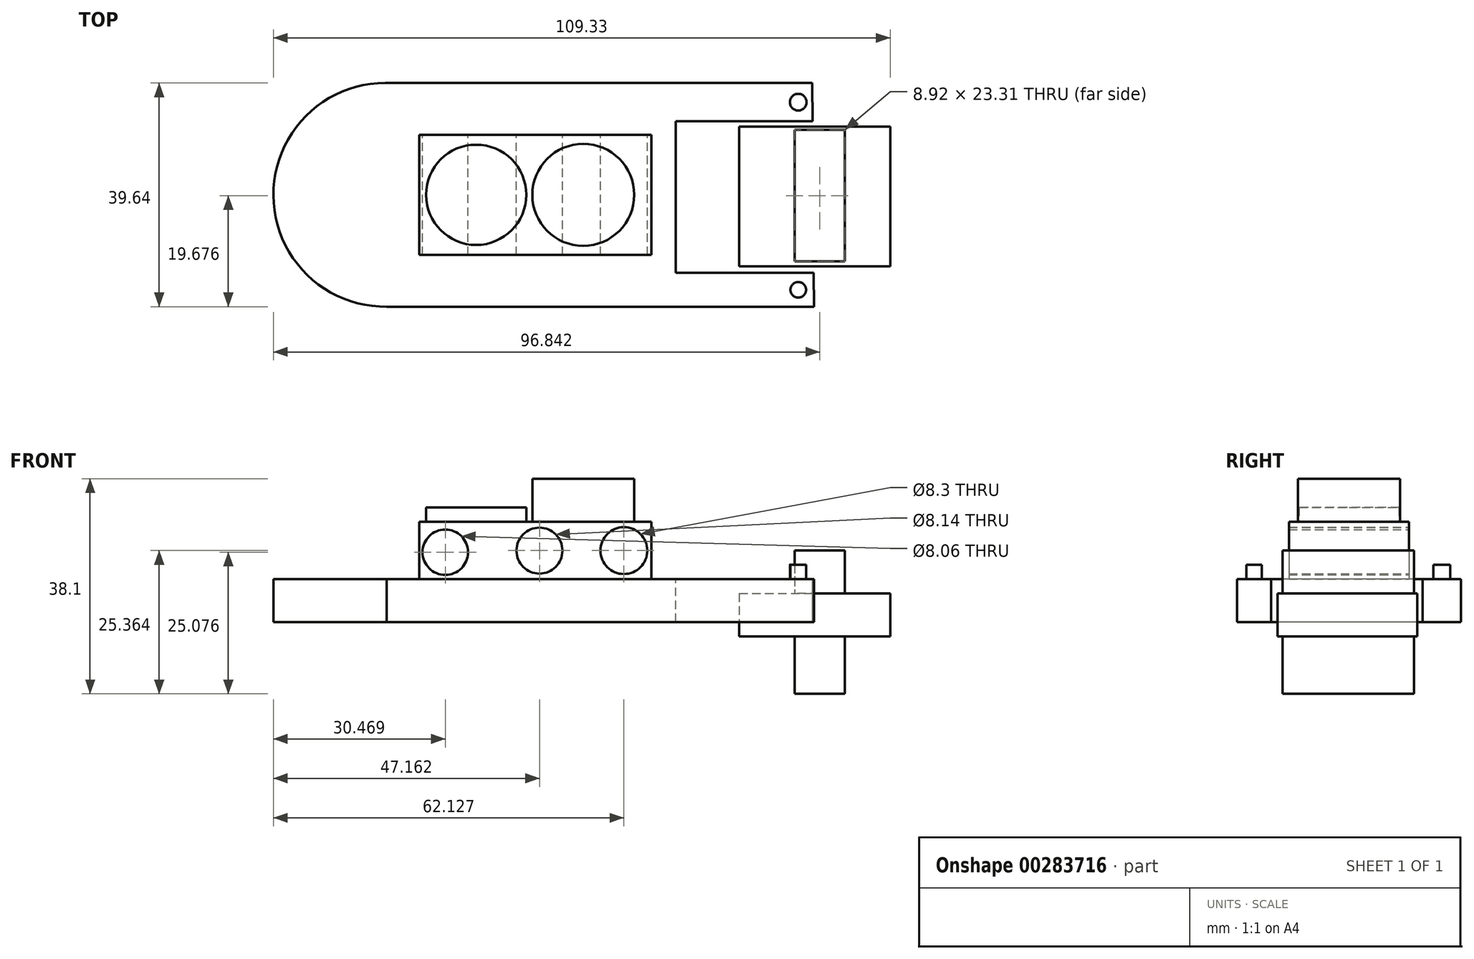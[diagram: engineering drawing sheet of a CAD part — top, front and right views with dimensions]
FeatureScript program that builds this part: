
annotation { "Feature Type Name" : "Feature", "Feature Type Description" : "" }
export const myFeature = defineFeature(function(context is Context, id is Id, definition is map)
    precondition{}
    {
        {
            var Q0;
            Q0=qCreatedBy(makeId("Top.planeOp"),FACE);
            var sketch = newSketch(context, id + "F0", { "sketchPlane" : qUnion([Q0])});
            skCircle(sketch, "E0", {"center": v(0, 0) * mm, "radius": 19.82 * mm});
            skLineSegment(sketch, "E1", {"start": v(0, 19.82) * mm, "end": v(75.7, 19.82) * mm});
            skLineSegment(sketch, "E2", {"start": v(-0.29, -19.82) * mm, "end": v(75.98, -19.82) * mm});
            skLineSegment(sketch, "E3", {"start": v(75.98, -19.82) * mm, "end": v(75.7, 19.82) * mm});
            skSolve(sketch);
        }
        {
            var Q0;
            Q0 = qSketchRegion(id + "F0", true);
            extrude(context, id + "F1", {"entities" : qUnion([Q0]), "depth" : 7.62 * mm});
        }
        {
            var Q0;
            Q0=makeQuery(id+"F1.opExtrude","CAP_FACE",FACE,{"disambiguationData":[OSD([sQuery(id+"F0.wireOp",EDGE,"E0"),sQuery(id+"F0.wireOp",EDGE,"E1"),sQuery(id+"F0.wireOp",EDGE,"E2"),sQuery(id+"F0.wireOp",EDGE,"E3")])],"isStart":false});
            var sketch = newSketch(context, id + "F2", { "sketchPlane" : qUnion([Q0])});
            skLineSegment(sketch, "E4.bottom", {"start": v(51.52, 12.95) * mm, "end": v(68.79, 12.95) * mm});
            skLineSegment(sketch, "E4.top", {"start": v(51.52, -13.81) * mm, "end": v(68.79, -13.81) * mm});
            skLineSegment(sketch, "E4.left", {"start": v(51.52, 12.95) * mm, "end": v(51.52, -13.81) * mm});
            skLineSegment(sketch, "E4.right", {"start": v(68.79, 12.95) * mm, "end": v(68.79, -13.81) * mm});
            skSolve(sketch);
        }
        {
            var Q0;
            Q0 = qSketchRegion(id + "F2", true);
            extrude(context, id + "F3", {"entities" : qUnion([Q0]), "operationType" : NewBodyOperationType.REMOVE, "oppositeDirection" : true, "depth" : 12.7 * mm});
        }
        {
            var Q0;
            Q0=qCreatedBy(makeId("Top.planeOp"),FACE);
            var sketch = newSketch(context, id + "F4", { "sketchPlane" : qUnion([Q0])});
            skLineSegment(sketch, "E5.bottom", {"start": v(6.04, 10.65) * mm, "end": v(47.2, 10.65) * mm});
            skLineSegment(sketch, "E5.top", {"start": v(6.04, -10.65) * mm, "end": v(47.2, -10.65) * mm});
            skLineSegment(sketch, "E5.left", {"start": v(6.04, 10.65) * mm, "end": v(6.04, -10.65) * mm});
            skLineSegment(sketch, "E5.right", {"start": v(47.2, 10.65) * mm, "end": v(47.2, -10.65) * mm});
            skSolve(sketch);
        }
        {
            var Q0;
            Q0 = qSketchRegion(id + "F4", true);
            extrude(context, id + "F5", {"entities" : qUnion([Q0]), "operationType" : NewBodyOperationType.ADD, "depth" : 17.78 * mm});
        }
        {
            var Q0;
            Q0=qCreatedBy(makeId("Top.planeOp"),FACE);
            var sketch = newSketch(context, id + "F6", { "sketchPlane" : qUnion([Q0])});
            skCircle(sketch, "E6", {"center": v(16.12, 0) * mm, "radius": 8.88 * mm});
            skSolve(sketch);
        }
        {
            var Q0;
            Q0 = qSketchRegion(id + "F6", true);
            extrude(context, id + "F7", {"entities" : qUnion([Q0]), "operationType" : NewBodyOperationType.ADD, "depth" : 20.32 * mm});
        }
        {
            var Q0;
            Q0=qCreatedBy(makeId("Top.planeOp"),FACE);
            var sketch = newSketch(context, id + "F8", { "sketchPlane" : qUnion([Q0])});
            skCircle(sketch, "E7", {"center": v(35.11, 0) * mm, "radius": 9.04 * mm});
            skSolve(sketch);
        }
        {
            var Q0;
            Q0 = qSketchRegion(id + "F8", true);
            extrude(context, id + "F9", {"entities" : qUnion([Q0]), "operationType" : NewBodyOperationType.ADD, "depth" : 25.4 * mm});
        }
        {
            var Q0;
            Q0=qCreatedBy(makeId("Front.planeOp"),FACE);
            var sketch = newSketch(context, id + "F10", { "sketchPlane" : qUnion([Q0])});
            skCircle(sketch, "E8", {"center": v(10.65, 12.38) * mm, "radius": 4.03 * mm});
            skCircle(sketch, "E9", {"center": v(27.34, 12.66) * mm, "radius": 4.07 * mm});
            skCircle(sketch, "E10", {"center": v(42.3, 12.66) * mm, "radius": 4.15 * mm});
            skSolve(sketch);
        }
        {
            var Q0;
            Q0 = qSketchRegion(id + "F10", true);
            extrude(context, id + "F11", {"entities" : qUnion([Q0]), "operationType" : NewBodyOperationType.REMOVE, "depth" : 25.4 * mm, "hasSecondDirection" : true, "secondDirectionOppositeDirection" : true, "secondDirectionDepth" : 25.4 * mm});
        }
        {
            var Q0;
            Q0=qCreatedBy(makeId("Top.planeOp"),FACE);
            var sketch = newSketch(context, id + "F12", { "sketchPlane" : qUnion([Q0])});
            skLineSegment(sketch, "E11.bottom", {"start": v(51.5, 13.03) * mm, "end": v(78.25, 13.03) * mm});
            skLineSegment(sketch, "E11.top", {"start": v(51.5, -13.83) * mm, "end": v(78.25, -13.83) * mm});
            skLineSegment(sketch, "E11.left", {"start": v(51.5, 13.03) * mm, "end": v(51.5, -13.83) * mm});
            skLineSegment(sketch, "E11.right", {"start": v(78.25, 13.03) * mm, "end": v(78.25, -13.83) * mm});
            skSolve(sketch);
        }
        {
            var Q0;
            Q0 = qSketchRegion(id + "F12", true);
            extrude(context, id + "F13", {"entities" : qUnion([Q0]), "operationType" : NewBodyOperationType.REMOVE, "oppositeDirection" : true, "depth" : 25.4 * mm, "hasSecondDirection" : true, "secondDirectionOppositeDirection" : false, "secondDirectionDepth" : 25.4 * mm});
        }
        {
            var Q0;
            Q0=qCreatedBy(makeId("Top.planeOp"),FACE);
            var sketch = newSketch(context, id + "F14", { "sketchPlane" : qUnion([Q0])});
            skCircle(sketch, "E12", {"center": v(73.22, -16.83) * mm, "radius": 1.4 * mm});
            skCircle(sketch, "E13", {"center": v(73.22, 16.43) * mm, "radius": 1.48 * mm});
            skSolve(sketch);
        }
        {
            var Q0;
            Q0 = qSketchRegion(id + "F14", true);
            extrude(context, id + "F15", {"entities" : qUnion([Q0]), "operationType" : NewBodyOperationType.ADD, "depth" : 10.16 * mm});
        }
        {
            var Q0;
            Q0=qCreatedBy(makeId("Top.planeOp"),FACE);
            var sketch = newSketch(context, id + "F16", { "sketchPlane" : qUnion([Q0])});
            skLineSegment(sketch, "E14.bottom", {"start": v(62.74, 12.09) * mm, "end": v(89.5, 12.09) * mm});
            skLineSegment(sketch, "E14.top", {"start": v(62.74, -12.66) * mm, "end": v(89.5, -12.66) * mm});
            skLineSegment(sketch, "E14.left", {"start": v(62.74, 12.09) * mm, "end": v(62.74, -12.66) * mm});
            skLineSegment(sketch, "E14.right", {"start": v(89.5, 12.09) * mm, "end": v(89.5, -12.66) * mm});
            skSolve(sketch);
        }
        {
            var Q0;
            Q0 = qSketchRegion(id + "F16", true);
            extrude(context, id + "F17", {"entities" : qUnion([Q0]), "depth" : 5.08 * mm, "hasSecondDirection" : true, "secondDirectionOppositeDirection" : true, "secondDirectionDepth" : 2.54 * mm});
        }
        {
            var Q0;
            Q0=qCreatedBy(makeId("Top.planeOp"),FACE);
            var sketch = newSketch(context, id + "F18", { "sketchPlane" : qUnion([Q0])});
            skLineSegment(sketch, "E15.bottom", {"start": v(72.56, -11.8) * mm, "end": v(81.48, -11.8) * mm});
            skLineSegment(sketch, "E15.top", {"start": v(72.56, 11.51) * mm, "end": v(81.48, 11.51) * mm});
            skLineSegment(sketch, "E15.left", {"start": v(72.56, -11.8) * mm, "end": v(72.56, 11.51) * mm});
            skLineSegment(sketch, "E15.right", {"start": v(81.48, -11.8) * mm, "end": v(81.48, 11.51) * mm});
            skSolve(sketch);
        }
        {
            var Q0;
            Q0 = qSketchRegion(id + "F18", true);
            extrude(context, id + "F19", {"entities" : qUnion([Q0]), "operationType" : NewBodyOperationType.ADD, "depth" : 12.7 * mm, "hasSecondDirection" : true, "secondDirectionOppositeDirection" : true, "secondDirectionDepth" : 12.7 * mm});
        }
    });
